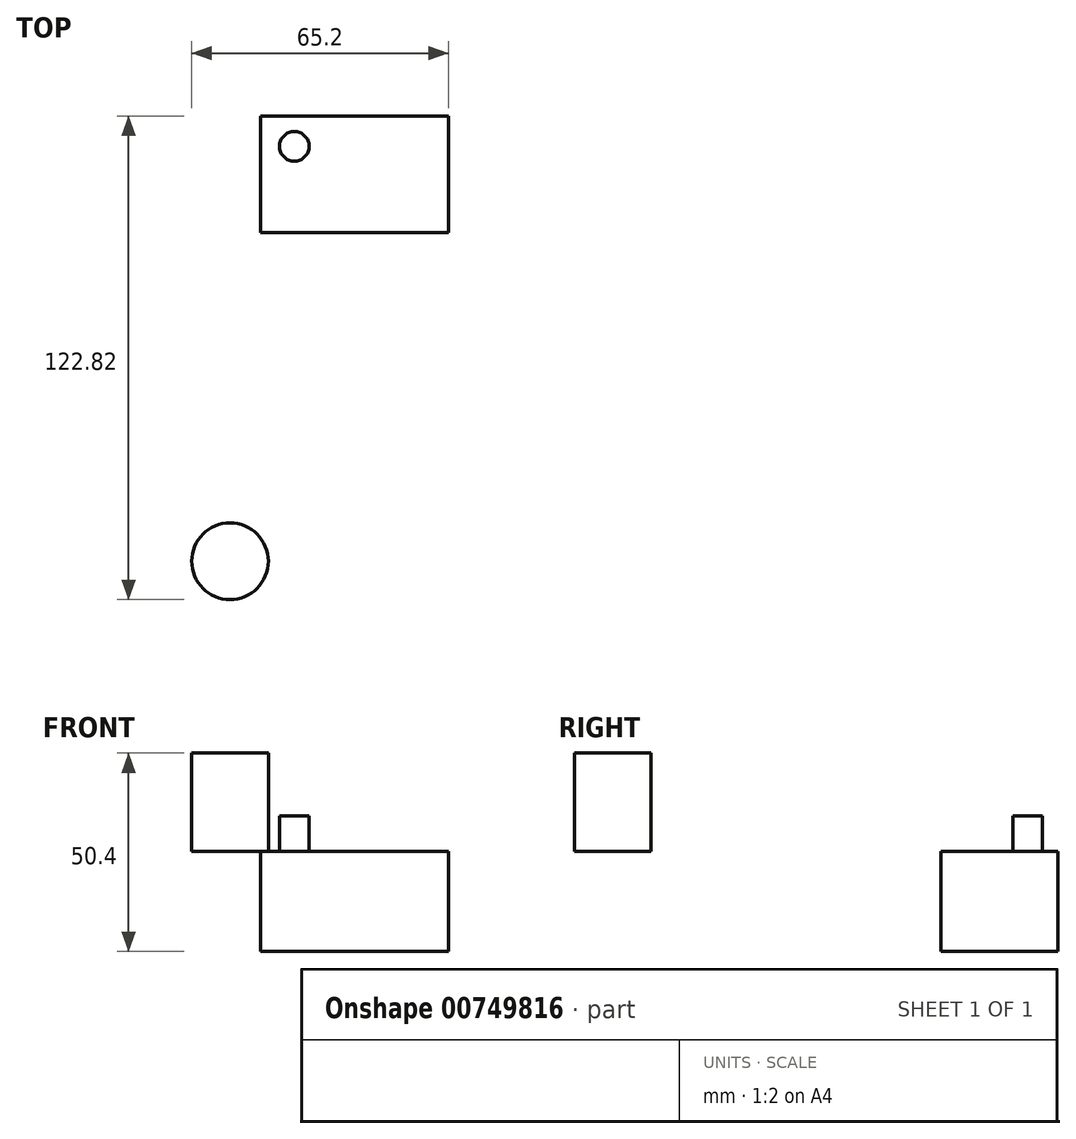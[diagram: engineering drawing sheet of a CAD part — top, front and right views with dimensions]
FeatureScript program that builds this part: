
annotation { "Feature Type Name" : "Feature", "Feature Type Description" : "" }
export const myFeature = defineFeature(function(context is Context, id is Id, definition is map)
    precondition{}
    {
        {
            var Q0;
            Q0=qCreatedBy(makeId("Top.planeOp"),FACE);
            var sketch = newSketch(context, id + "F0", { "sketchPlane" : qUnion([Q0])});
            skLineSegment(sketch, "E0.bottom", {"start": v(-135.59, -43.8) * mm, "end": v(-87.83, -43.8) * mm});
            skLineSegment(sketch, "E0.top", {"start": v(-135.59, -14.16) * mm, "end": v(-87.83, -14.16) * mm});
            skLineSegment(sketch, "E0.left", {"start": v(-135.59, -43.8) * mm, "end": v(-135.59, -14.16) * mm});
            skLineSegment(sketch, "E0.right", {"start": v(-87.83, -43.8) * mm, "end": v(-87.83, -14.16) * mm});
            skSolve(sketch);
        }
        {
            var Q0;
            Q0=makeQuery(id+"F0.imprint","IMPRINT",FACE,{"disambiguationData":[TD([[makeQuery(id+"F0.imprint","IMPRINT",EDGE,{"derivedFrom":sQuery(id+"F0.wireOp",EDGE,"E0.bottom")}),1.0]])]});
            extrude(context, id + "F1", {"entities" : qUnion([Q0]), "depth" : 25.4 * mm, "offsetDistance" : 25.4 * mm});
        }
        {
            var Q0;
            Q0=makeQuery(id+"F1.opExtrude","CAP_FACE",FACE,{"disambiguationData":[OSD([sQuery(id+"F0.wireOp",EDGE,"E0.bottom"),sQuery(id+"F0.wireOp",EDGE,"E0.top"),sQuery(id+"F0.wireOp",EDGE,"E0.left"),sQuery(id+"F0.wireOp",EDGE,"E0.right")])],"isStart":false});
            var sketch = newSketch(context, id + "F2", { "sketchPlane" : qUnion([Q0])});
            skPoint(sketch, "E1.centerSnap0", {"position": v(-135.59, -28.98) * mm});
            skPoint(sketch, "E1.perimeterSnap0", {"position": v(-111.71, -43.8) * mm});
            skPoint(sketch, "E1.perimeterSnap1", {"position": v(-135.59, -28.98) * mm});
            skCircle(sketch, "E2", {"center": v(-143.3, -127.25) * mm, "radius": 9.73 * mm});
            skSolve(sketch);
        }
        {
            var Q0;
            Q0=makeQuery(id+"F2.imprint","IMPRINT",FACE,{"disambiguationData":[TD([[makeQuery(id+"F2.imprint","IMPRINT",EDGE,{"derivedFrom":sQuery(id+"F2.wireOp",EDGE,"E2")}),1.0]])]});
            extrude(context, id + "F3", {"entities" : qUnion([Q0]), "depth" : 25 * mm, "offsetDistance" : 25 * mm});
        }
        {
            var Q0;
            Q0=makeQuery(id+"F1.opExtrude","CAP_FACE",FACE,{"disambiguationData":[OSD([sQuery(id+"F0.wireOp",EDGE,"E0.bottom"),sQuery(id+"F0.wireOp",EDGE,"E0.top"),sQuery(id+"F0.wireOp",EDGE,"E0.left"),sQuery(id+"F0.wireOp",EDGE,"E0.right")])],"isStart":false});
            var sketch = newSketch(context, id + "F4", { "sketchPlane" : qUnion([Q0])});
            skSolve(sketch);
        }
        {
            var Q0;
            Q0=makeQuery(id+"F4.imprint","IMPRINT",FACE,{"disambiguationData":[TD([[makeQuery(id+"F4.imprint","IMPRINT",EDGE,{"derivedFrom":makeQuery(id+"F1.opExtrude","CAP_EDGE",EDGE,{"disambiguationData":[OSD([sQuery(id+"F0.wireOp",EDGE,"E0.bottom")])],"isStart":false})}),1.0]])]});
            var sketch = newSketch(context, id + "F5", { "sketchPlane" : qUnion([Q0])});
            skCircle(sketch, "E3", {"center": v(-126.96, -21.84) * mm, "radius": 3.77 * mm});
            skSolve(sketch);
        }
        {
            var Q0;
            Q0 = qSketchRegion(id + "F5", true);
            extrude(context, id + "F6", {"entities" : qUnion([Q0]), "operationType" : NewBodyOperationType.ADD, "depth" : 9 * mm, "offsetDistance" : 25 * mm});
        }
    });
